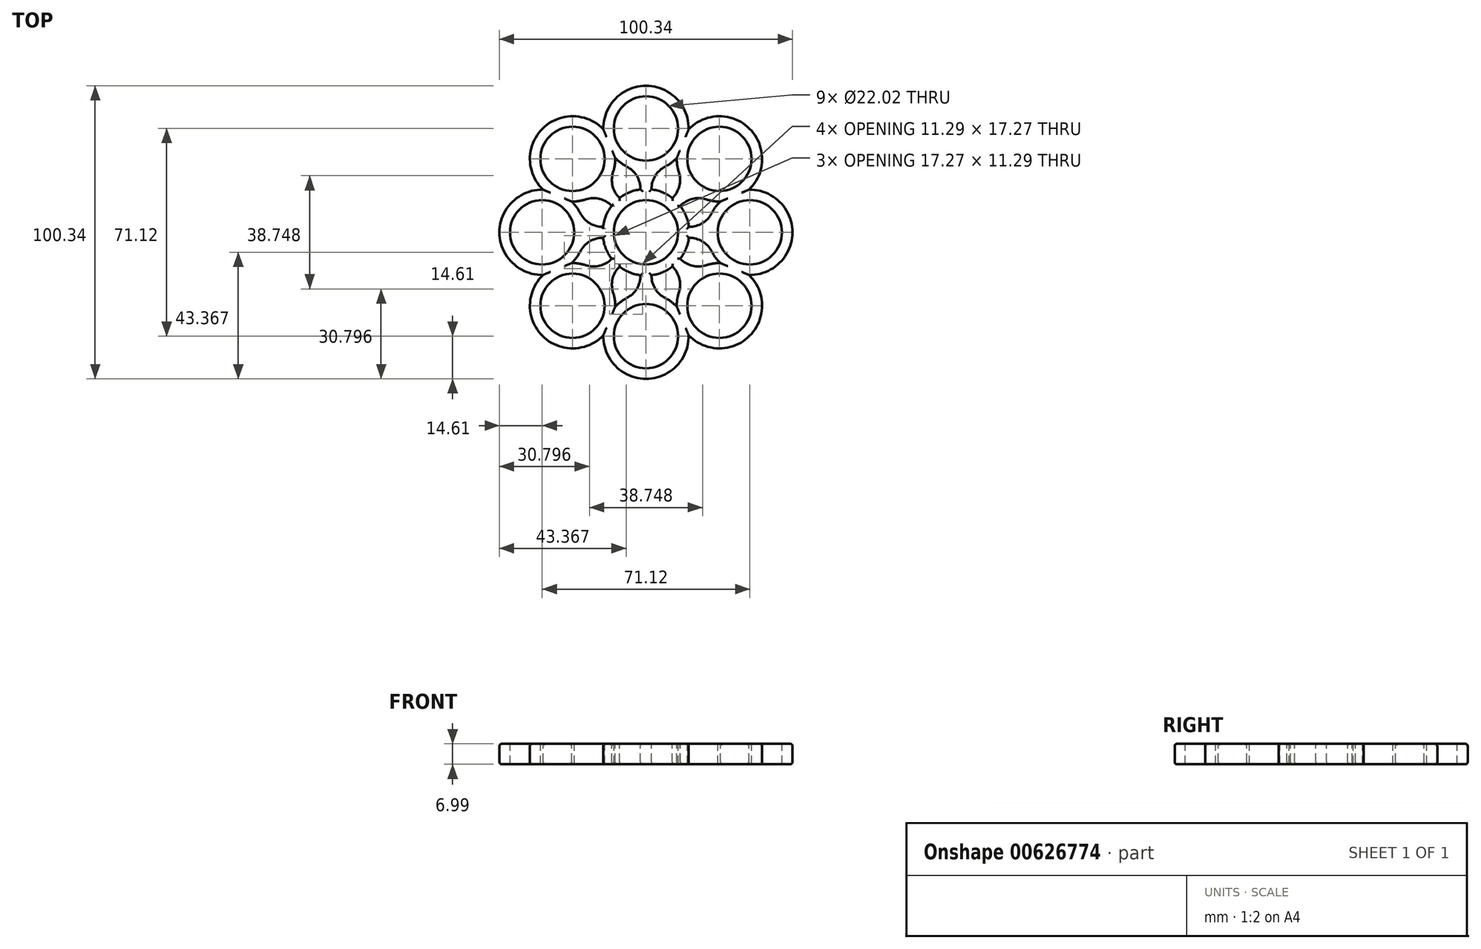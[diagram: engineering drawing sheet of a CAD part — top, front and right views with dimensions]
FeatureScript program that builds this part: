
annotation { "Feature Type Name" : "Feature", "Feature Type Description" : "" }
export const myFeature = defineFeature(function(context is Context, id is Id, definition is map)
    precondition{}
    {
        {
            var Q0;
            Q0=qCreatedBy(makeId("Top.planeOp"),FACE);
            var sketch = newSketch(context, id + "F0", { "sketchPlane" : qUnion([Q0])});
            skCircle(sketch, "E0", {"center": v(0, 0) * mm, "radius": 11.01 * mm});
            skLineSegment(sketch, "E1", {"start": v(0, 0) * mm, "end": v(0, -35.56) * mm});
            skLineSegment(sketch, "E2", {"start": v(0, 0) * mm, "end": v(0, 35.56) * mm});
            skLineSegment(sketch, "E3", {"start": v(0, 0) * mm, "end": v(25.14, 25.14) * mm});
            skLineSegment(sketch, "E4", {"start": v(0, 0) * mm, "end": v(-25.14, -25.14) * mm});
            skLineSegment(sketch, "E5", {"start": v(0, 0) * mm, "end": v(25.14, -25.14) * mm});
            skLineSegment(sketch, "E6", {"start": v(0, 0) * mm, "end": v(-25.14, 25.14) * mm});
            skLineSegment(sketch, "E7", {"start": v(0, 0) * mm, "end": v(35.56, 0) * mm});
            skLineSegment(sketch, "E8", {"start": v(0, 0) * mm, "end": v(-35.56, 0) * mm});
            skCircle(sketch, "E9", {"center": v(0, 35.56) * mm, "radius": 11.01 * mm});
            skCircle(sketch, "E10", {"center": v(25.14, 25.14) * mm, "radius": 11.01 * mm});
            skCircle(sketch, "E11", {"center": v(35.56, 0) * mm, "radius": 11.01 * mm});
            skCircle(sketch, "E12", {"center": v(25.14, -25.14) * mm, "radius": 11.01 * mm});
            skCircle(sketch, "E13", {"center": v(0, -35.56) * mm, "radius": 11.01 * mm});
            skCircle(sketch, "E14", {"center": v(-25.14, -25.14) * mm, "radius": 11.01 * mm});
            skCircle(sketch, "E15", {"center": v(-35.56, 0) * mm, "radius": 11.01 * mm});
            skCircle(sketch, "E16", {"center": v(-25.14, 25.14) * mm, "radius": 11.01 * mm});
            skCircle(sketch, "E17", {"center": v(0, 35.56) * mm, "radius": 14.6 * mm});
            skCircle(sketch, "E18", {"center": v(-25.14, 25.14) * mm, "radius": 14.6 * mm});
            skCircle(sketch, "E19", {"center": v(25.14, 25.14) * mm, "radius": 14.6 * mm});
            skCircle(sketch, "E20", {"center": v(35.56, 0) * mm, "radius": 14.6 * mm});
            skCircle(sketch, "E21", {"center": v(25.14, -25.14) * mm, "radius": 14.6 * mm});
            skCircle(sketch, "E22", {"center": v(0, -35.56) * mm, "radius": 14.6 * mm});
            skCircle(sketch, "E23", {"center": v(-35.56, 0) * mm, "radius": 14.6 * mm});
            skCircle(sketch, "E24", {"center": v(-25.14, -25.14) * mm, "radius": 14.6 * mm});
            skCircle(sketch, "E25", {"center": v(0, 0) * mm, "radius": 14.82 * mm});
            skArc(sketch, "E26", {"start": v(-11.74, 9.05) * mm, "mid": v(-15.85, 11.43) * mm, "end": v(-20.6, 11.26) * mm});
            skArc(sketch, "E27", {"start": v(-11.26, 20.6) * mm, "mid": v(-11.43, 15.85) * mm, "end": v(-9.05, 11.74) * mm});
            skArc(sketch, "E28.1.0", {"start": v(-22.53, 6.6) * mm, "mid": v(-19.3, 3.13) * mm, "end": v(-14.7, 1.9) * mm});
            skArc(sketch, "E28.1.1", {"start": v(-14.7, -1.9) * mm, "mid": v(-19.3, -3.13) * mm, "end": v(-22.53, -6.6) * mm});
            skArc(sketch, "E28.2.0", {"start": v(-20.6, -11.26) * mm, "mid": v(-15.85, -11.43) * mm, "end": v(-11.74, -9.05) * mm});
            skArc(sketch, "E28.2.1", {"start": v(-9.05, -11.74) * mm, "mid": v(-11.43, -15.85) * mm, "end": v(-11.26, -20.6) * mm});
            skArc(sketch, "E28.3.0", {"start": v(-6.6, -22.53) * mm, "mid": v(-3.13, -19.3) * mm, "end": v(-1.9, -14.7) * mm});
            skArc(sketch, "E28.3.1", {"start": v(1.9, -14.7) * mm, "mid": v(3.13, -19.3) * mm, "end": v(6.6, -22.53) * mm});
            skArc(sketch, "E28.4.0", {"start": v(11.26, -20.6) * mm, "mid": v(11.43, -15.85) * mm, "end": v(9.05, -11.74) * mm});
            skArc(sketch, "E28.4.1", {"start": v(11.74, -9.05) * mm, "mid": v(15.85, -11.43) * mm, "end": v(20.6, -11.26) * mm});
            skArc(sketch, "E28.5.0", {"start": v(22.53, -6.6) * mm, "mid": v(19.3, -3.13) * mm, "end": v(14.7, -1.9) * mm});
            skArc(sketch, "E28.5.1", {"start": v(14.7, 1.9) * mm, "mid": v(19.3, 3.13) * mm, "end": v(22.53, 6.6) * mm});
            skArc(sketch, "E28.6.0", {"start": v(20.6, 11.26) * mm, "mid": v(15.85, 11.43) * mm, "end": v(11.74, 9.05) * mm});
            skArc(sketch, "E28.6.1", {"start": v(9.05, 11.74) * mm, "mid": v(11.43, 15.85) * mm, "end": v(11.26, 20.6) * mm});
            skArc(sketch, "E28.7.0", {"start": v(6.6, 22.53) * mm, "mid": v(3.13, 19.3) * mm, "end": v(1.9, 14.7) * mm});
            skArc(sketch, "E28.7.1", {"start": v(-1.9, 14.7) * mm, "mid": v(-3.13, 19.3) * mm, "end": v(-6.6, 22.53) * mm});
            skSolve(sketch);
        }
        {
            var Q0;
            Q0 = qSketchRegion(id + "F0", true);
            var Q1;
            {var subQ1=sQuery(id+"F0.wireOp",EDGE,"E0");var subQ5=sQuery(id+"F0.wireOp",EDGE,"E2");var subQ6=makeQuery(id+"F0.imprint","INTERSECT",VERTEX,{"derivedFrom":[subQ1,subQ5]});Q1=makeQuery(id+"F0.imprint","IMPRINT",FACE,{"disambiguationData":[TD([[makeQuery(id+"F0.imprint","IMPRINT",EDGE,{"disambiguationData":[TD([[subQ6,-1.0]])],"derivedFrom":subQ1}),-1.0]])]});}
            var Q2;
            {var subQ2=sQuery(id+"F0.wireOp",EDGE,"E3");var subQ4=sQuery(id+"F0.wireOp",EDGE,"E0");var subQ5=makeQuery(id+"F0.imprint","INTERSECT",VERTEX,{"derivedFrom":[subQ4,subQ2]});Q2=makeQuery(id+"F0.imprint","IMPRINT",FACE,{"disambiguationData":[TD([[makeQuery(id+"F0.imprint","IMPRINT",EDGE,{"disambiguationData":[TD([[subQ5,-1.0]])],"derivedFrom":subQ4}),-1.0]])]});}
            var Q3;
            {var subQ5=sQuery(id+"F0.wireOp",EDGE,"E28.6.0");Q3=makeQuery(id+"F0.imprint","IMPRINT",FACE,{"disambiguationData":[TD([[makeQuery(id+"F0.imprint","IMPRINT",EDGE,{"derivedFrom":subQ5}),-1.0]])]});}
            var Q4;
            {var subQ5=sQuery(id+"F0.wireOp",EDGE,"E28.6.1");Q4=makeQuery(id+"F0.imprint","IMPRINT",FACE,{"disambiguationData":[TD([[makeQuery(id+"F0.imprint","IMPRINT",EDGE,{"derivedFrom":subQ5}),-1.0]])]});}
            var Q5;
            {var subQ5=sQuery(id+"F0.wireOp",EDGE,"E28.5.1");Q5=makeQuery(id+"F0.imprint","IMPRINT",FACE,{"disambiguationData":[TD([[makeQuery(id+"F0.imprint","IMPRINT",EDGE,{"derivedFrom":subQ5}),-1.0]])]});}
            var Q6;
            {var subQ5=sQuery(id+"F0.wireOp",EDGE,"E28.5.0");Q6=makeQuery(id+"F0.imprint","IMPRINT",FACE,{"disambiguationData":[TD([[makeQuery(id+"F0.imprint","IMPRINT",EDGE,{"derivedFrom":subQ5}),-1.0]])]});}
            var Q7;
            {var subQ1=sQuery(id+"F0.wireOp",EDGE,"E0");var subQ6=sQuery(id+"F0.wireOp",EDGE,"E7");var subQ7=makeQuery(id+"F0.imprint","INTERSECT",VERTEX,{"derivedFrom":[subQ1,subQ6]});Q7=makeQuery(id+"F0.imprint","IMPRINT",FACE,{"disambiguationData":[TD([[makeQuery(id+"F0.imprint","IMPRINT",EDGE,{"disambiguationData":[TD([[subQ7,1.0]])],"derivedFrom":subQ1}),-1.0]])]});}
            var Q8;
            {var subQ4=sQuery(id+"F0.wireOp",EDGE,"E0");var subQ6=sQuery(id+"F0.wireOp",EDGE,"E3");var subQ7=makeQuery(id+"F0.imprint","INTERSECT",VERTEX,{"derivedFrom":[subQ4,subQ6]});Q8=makeQuery(id+"F0.imprint","IMPRINT",FACE,{"disambiguationData":[TD([[makeQuery(id+"F0.imprint","IMPRINT",EDGE,{"disambiguationData":[TD([[subQ7,1.0]])],"derivedFrom":subQ4}),-1.0]])]});}
            var Q9;
            {var subQ5=sQuery(id+"F0.wireOp",EDGE,"E28.4.1");Q9=makeQuery(id+"F0.imprint","IMPRINT",FACE,{"disambiguationData":[TD([[makeQuery(id+"F0.imprint","IMPRINT",EDGE,{"derivedFrom":subQ5}),-1.0]])]});}
            var Q10;
            {var subQ5=sQuery(id+"F0.wireOp",EDGE,"E28.4.0");Q10=makeQuery(id+"F0.imprint","IMPRINT",FACE,{"disambiguationData":[TD([[makeQuery(id+"F0.imprint","IMPRINT",EDGE,{"derivedFrom":subQ5}),-1.0]])]});}
            var Q11;
            {var subQ5=sQuery(id+"F0.wireOp",EDGE,"E28.3.1");Q11=makeQuery(id+"F0.imprint","IMPRINT",FACE,{"disambiguationData":[TD([[makeQuery(id+"F0.imprint","IMPRINT",EDGE,{"derivedFrom":subQ5}),-1.0]])]});}
            var Q12;
            {var subQ5=sQuery(id+"F0.wireOp",EDGE,"E28.3.0");Q12=makeQuery(id+"F0.imprint","IMPRINT",FACE,{"disambiguationData":[TD([[makeQuery(id+"F0.imprint","IMPRINT",EDGE,{"derivedFrom":subQ5}),-1.0]])]});}
            var Q13;
            {var subQ5=sQuery(id+"F0.wireOp",EDGE,"E28.2.1");Q13=makeQuery(id+"F0.imprint","IMPRINT",FACE,{"disambiguationData":[TD([[makeQuery(id+"F0.imprint","IMPRINT",EDGE,{"derivedFrom":subQ5}),-1.0]])]});}
            var Q14;
            {var subQ5=sQuery(id+"F0.wireOp",EDGE,"E28.2.0");Q14=makeQuery(id+"F0.imprint","IMPRINT",FACE,{"disambiguationData":[TD([[makeQuery(id+"F0.imprint","IMPRINT",EDGE,{"derivedFrom":subQ5}),-1.0]])]});}
            var Q15;
            {var subQ5=sQuery(id+"F0.wireOp",EDGE,"E28.1.1");Q15=makeQuery(id+"F0.imprint","IMPRINT",FACE,{"disambiguationData":[TD([[makeQuery(id+"F0.imprint","IMPRINT",EDGE,{"derivedFrom":subQ5}),-1.0]])]});}
            var Q16;
            {var subQ5=sQuery(id+"F0.wireOp",EDGE,"E28.1.0");Q16=makeQuery(id+"F0.imprint","IMPRINT",FACE,{"disambiguationData":[TD([[makeQuery(id+"F0.imprint","IMPRINT",EDGE,{"derivedFrom":subQ5}),-1.0]])]});}
            var Q17;
            {var subQ5=sQuery(id+"F0.wireOp",EDGE,"E26");Q17=makeQuery(id+"F0.imprint","IMPRINT",FACE,{"disambiguationData":[TD([[makeQuery(id+"F0.imprint","IMPRINT",EDGE,{"derivedFrom":subQ5}),-1.0]])]});}
            var Q18;
            {var subQ5=sQuery(id+"F0.wireOp",EDGE,"E27");Q18=makeQuery(id+"F0.imprint","IMPRINT",FACE,{"disambiguationData":[TD([[makeQuery(id+"F0.imprint","IMPRINT",EDGE,{"derivedFrom":subQ5}),-1.0]])]});}
            var Q19;
            {var subQ5=sQuery(id+"F0.wireOp",EDGE,"E28.7.1");Q19=makeQuery(id+"F0.imprint","IMPRINT",FACE,{"disambiguationData":[TD([[makeQuery(id+"F0.imprint","IMPRINT",EDGE,{"derivedFrom":subQ5}),-1.0]])]});}
            var Q20;
            {var subQ2=sQuery(id+"F0.wireOp",EDGE,"E6");var subQ5=sQuery(id+"F0.wireOp",EDGE,"E0");var subQ9=makeQuery(id+"F0.imprint","INTERSECT",VERTEX,{"derivedFrom":[subQ5,subQ2]});Q20=makeQuery(id+"F0.imprint","IMPRINT",FACE,{"disambiguationData":[TD([[makeQuery(id+"F0.imprint","IMPRINT",EDGE,{"disambiguationData":[TD([[subQ9,-1.0]])],"derivedFrom":subQ5}),-1.0]])]});}
            var Q21;
            {var subQ0=sQuery(id+"F0.wireOp",EDGE,"E8");var subQ1=sQuery(id+"F0.wireOp",EDGE,"E0");var subQ2=makeQuery(id+"F0.imprint","INTERSECT",VERTEX,{"derivedFrom":[subQ1,subQ0]});Q21=makeQuery(id+"F0.imprint","IMPRINT",FACE,{"disambiguationData":[TD([[makeQuery(id+"F0.imprint","IMPRINT",EDGE,{"disambiguationData":[TD([[subQ2,-1.0]])],"derivedFrom":subQ1}),-1.0]])]});}
            var Q22;
            {var subQ2=sQuery(id+"F0.wireOp",EDGE,"E4");var subQ4=sQuery(id+"F0.wireOp",EDGE,"E0");var subQ5=makeQuery(id+"F0.imprint","INTERSECT",VERTEX,{"derivedFrom":[subQ4,subQ2]});Q22=makeQuery(id+"F0.imprint","IMPRINT",FACE,{"disambiguationData":[TD([[makeQuery(id+"F0.imprint","IMPRINT",EDGE,{"disambiguationData":[TD([[subQ5,-1.0]])],"derivedFrom":subQ4}),-1.0]])]});}
            var Q23;
            {var subQ2=sQuery(id+"F0.wireOp",EDGE,"E1");var subQ4=sQuery(id+"F0.wireOp",EDGE,"E0");var subQ5=makeQuery(id+"F0.imprint","INTERSECT",VERTEX,{"derivedFrom":[subQ4,subQ2]});Q23=makeQuery(id+"F0.imprint","IMPRINT",FACE,{"disambiguationData":[TD([[makeQuery(id+"F0.imprint","IMPRINT",EDGE,{"disambiguationData":[TD([[subQ5,-1.0]])],"derivedFrom":subQ4}),-1.0]])]});}
            var Q24;
            {var subQ5=sQuery(id+"F0.wireOp",EDGE,"E28.7.0");Q24=makeQuery(id+"F0.imprint","IMPRINT",FACE,{"disambiguationData":[TD([[makeQuery(id+"F0.imprint","IMPRINT",EDGE,{"derivedFrom":subQ5}),-1.0]])]});}
            extrude(context, id + "F1", {"entities" : qUnion([Q0, Q1, Q2, Q3, Q4, Q5, Q6, Q7, Q8, Q9, Q10, Q11, Q12, Q13, Q14, Q15, Q16, Q17, Q18, Q19, Q20, Q21, Q22, Q23, Q24]), "oppositeDirection" : true, "depth" : 7 * mm, "offsetDistance" : 25.4 * mm});
        }
        {
            var Q0;
            {var subQ0=sQuery(id+"F0.wireOp",EDGE,"E18");Q0=makeQuery(id+"F1.opExtrude","CAP_EDGE",EDGE,{"disambiguationData":[OSD([subQ0]),TDD([makeQuery(id+"F0.imprint","IMPRINT",EDGE,{"disambiguationData":[TD([[makeQuery(id+"F0.imprint","INTERSECT",VERTEX,{"disambiguationData":[OD(0.0)],"derivedFrom":[sQuery(id+"F0.wireOp",EDGE,"E17"),subQ0]}),-1.0]])],"derivedFrom":subQ0})])],"isStart":true});}
            var Q1;
            {var subQ0=sQuery(id+"F0.wireOp",EDGE,"E17");Q1=makeQuery(id+"F1.opExtrude","CAP_EDGE",EDGE,{"disambiguationData":[OSD([subQ0]),TDD([makeQuery(id+"F0.imprint","IMPRINT",EDGE,{"disambiguationData":[TD([[makeQuery(id+"F0.imprint","INTERSECT",VERTEX,{"disambiguationData":[OD(0.0)],"derivedFrom":[subQ0,sQuery(id+"F0.wireOp",EDGE,"E18")]}),1.0]])],"derivedFrom":subQ0})])],"isStart":true});}
            var Q2;
            {var subQ0=sQuery(id+"F0.wireOp",EDGE,"E19");Q2=makeQuery(id+"F1.opExtrude","CAP_EDGE",EDGE,{"disambiguationData":[OSD([subQ0]),TDD([makeQuery(id+"F0.imprint","IMPRINT",EDGE,{"disambiguationData":[TD([[makeQuery(id+"F0.imprint","INTERSECT",VERTEX,{"disambiguationData":[OD(0.0)],"derivedFrom":[sQuery(id+"F0.wireOp",EDGE,"E17"),subQ0]}),1.0]])],"derivedFrom":subQ0})])],"isStart":true});}
            var Q3;
            {var subQ0=sQuery(id+"F0.wireOp",EDGE,"E20");Q3=makeQuery(id+"F1.opExtrude","CAP_EDGE",EDGE,{"disambiguationData":[OSD([subQ0]),TDD([makeQuery(id+"F0.imprint","IMPRINT",EDGE,{"disambiguationData":[TD([[makeQuery(id+"F0.imprint","INTERSECT",VERTEX,{"disambiguationData":[OD(0.0)],"derivedFrom":[sQuery(id+"F0.wireOp",EDGE,"E19"),subQ0]}),1.0]])],"derivedFrom":subQ0})])],"isStart":true});}
            var Q4;
            {var subQ0=sQuery(id+"F0.wireOp",EDGE,"E21");Q4=makeQuery(id+"F1.opExtrude","CAP_EDGE",EDGE,{"disambiguationData":[OSD([subQ0]),TDD([makeQuery(id+"F0.imprint","IMPRINT",EDGE,{"disambiguationData":[TD([[makeQuery(id+"F0.imprint","INTERSECT",VERTEX,{"disambiguationData":[OD(0.0)],"derivedFrom":[sQuery(id+"F0.wireOp",EDGE,"E20"),subQ0]}),1.0]])],"derivedFrom":subQ0})])],"isStart":true});}
            var Q5;
            {var subQ0=sQuery(id+"F0.wireOp",EDGE,"E22");Q5=makeQuery(id+"F1.opExtrude","CAP_EDGE",EDGE,{"disambiguationData":[OSD([subQ0]),TDD([makeQuery(id+"F0.imprint","IMPRINT",EDGE,{"disambiguationData":[TD([[makeQuery(id+"F0.imprint","INTERSECT",VERTEX,{"disambiguationData":[OD(0.0)],"derivedFrom":[sQuery(id+"F0.wireOp",EDGE,"E21"),subQ0]}),1.0]])],"derivedFrom":subQ0})])],"isStart":true});}
            var Q6;
            {var subQ0=sQuery(id+"F0.wireOp",EDGE,"E24");Q6=makeQuery(id+"F1.opExtrude","CAP_EDGE",EDGE,{"disambiguationData":[OSD([subQ0]),TDD([makeQuery(id+"F0.imprint","IMPRINT",EDGE,{"disambiguationData":[TD([[makeQuery(id+"F0.imprint","INTERSECT",VERTEX,{"disambiguationData":[OD(0.0)],"derivedFrom":[sQuery(id+"F0.wireOp",EDGE,"E22"),subQ0]}),1.0]])],"derivedFrom":subQ0})])],"isStart":true});}
            var Q7;
            {var subQ0=sQuery(id+"F0.wireOp",EDGE,"E23");Q7=makeQuery(id+"F1.opExtrude","CAP_EDGE",EDGE,{"disambiguationData":[OSD([subQ0]),TDD([makeQuery(id+"F0.imprint","IMPRINT",EDGE,{"disambiguationData":[TD([[makeQuery(id+"F0.imprint","INTERSECT",VERTEX,{"disambiguationData":[OD(0.0)],"derivedFrom":[sQuery(id+"F0.wireOp",EDGE,"E18"),subQ0]}),-1.0]])],"derivedFrom":subQ0})])],"isStart":true});}
            fillet(context, id + "F2", {"entities" : qUnion([Q0, Q1, Q2, Q3, Q4, Q5, Q6, Q7]), "radius" : 0.76 * mm, "tangentPropagation" : true, "allowEdgeOverflow" : false});
        }
        {
            var Q0;
            {var subQ0=sQuery(id+"F0.wireOp",EDGE,"E21");Q0=makeQuery(id+"F1.opExtrude","CAP_EDGE",EDGE,{"disambiguationData":[OSD([subQ0]),TDD([makeQuery(id+"F0.imprint","IMPRINT",EDGE,{"disambiguationData":[TD([[makeQuery(id+"F0.imprint","INTERSECT",VERTEX,{"disambiguationData":[OD(0.0)],"derivedFrom":[sQuery(id+"F0.wireOp",EDGE,"E20"),subQ0]}),1.0]])],"derivedFrom":subQ0})])],"isStart":false});}
            var Q1;
            {var subQ0=sQuery(id+"F0.wireOp",EDGE,"E20");Q1=makeQuery(id+"F1.opExtrude","CAP_EDGE",EDGE,{"disambiguationData":[OSD([subQ0]),TDD([makeQuery(id+"F0.imprint","IMPRINT",EDGE,{"disambiguationData":[TD([[makeQuery(id+"F0.imprint","INTERSECT",VERTEX,{"disambiguationData":[OD(0.0)],"derivedFrom":[sQuery(id+"F0.wireOp",EDGE,"E19"),subQ0]}),1.0]])],"derivedFrom":subQ0})])],"isStart":false});}
            var Q2;
            {var subQ0=sQuery(id+"F0.wireOp",EDGE,"E19");Q2=makeQuery(id+"F1.opExtrude","CAP_EDGE",EDGE,{"disambiguationData":[OSD([subQ0]),TDD([makeQuery(id+"F0.imprint","IMPRINT",EDGE,{"disambiguationData":[TD([[makeQuery(id+"F0.imprint","INTERSECT",VERTEX,{"disambiguationData":[OD(0.0)],"derivedFrom":[sQuery(id+"F0.wireOp",EDGE,"E17"),subQ0]}),1.0]])],"derivedFrom":subQ0})])],"isStart":false});}
            var Q3;
            {var subQ0=sQuery(id+"F0.wireOp",EDGE,"E17");Q3=makeQuery(id+"F1.opExtrude","CAP_EDGE",EDGE,{"disambiguationData":[OSD([subQ0]),TDD([makeQuery(id+"F0.imprint","IMPRINT",EDGE,{"disambiguationData":[TD([[makeQuery(id+"F0.imprint","INTERSECT",VERTEX,{"disambiguationData":[OD(0.0)],"derivedFrom":[subQ0,sQuery(id+"F0.wireOp",EDGE,"E18")]}),1.0]])],"derivedFrom":subQ0})])],"isStart":false});}
            var Q4;
            {var subQ0=sQuery(id+"F0.wireOp",EDGE,"E18");Q4=makeQuery(id+"F1.opExtrude","CAP_EDGE",EDGE,{"disambiguationData":[OSD([subQ0]),TDD([makeQuery(id+"F0.imprint","IMPRINT",EDGE,{"disambiguationData":[TD([[makeQuery(id+"F0.imprint","INTERSECT",VERTEX,{"disambiguationData":[OD(0.0)],"derivedFrom":[sQuery(id+"F0.wireOp",EDGE,"E17"),subQ0]}),-1.0]])],"derivedFrom":subQ0})])],"isStart":false});}
            var Q5;
            {var subQ0=sQuery(id+"F0.wireOp",EDGE,"E23");Q5=makeQuery(id+"F1.opExtrude","CAP_EDGE",EDGE,{"disambiguationData":[OSD([subQ0]),TDD([makeQuery(id+"F0.imprint","IMPRINT",EDGE,{"disambiguationData":[TD([[makeQuery(id+"F0.imprint","INTERSECT",VERTEX,{"disambiguationData":[OD(0.0)],"derivedFrom":[sQuery(id+"F0.wireOp",EDGE,"E18"),subQ0]}),-1.0]])],"derivedFrom":subQ0})])],"isStart":false});}
            var Q6;
            {var subQ0=sQuery(id+"F0.wireOp",EDGE,"E24");Q6=makeQuery(id+"F1.opExtrude","CAP_EDGE",EDGE,{"disambiguationData":[OSD([subQ0]),TDD([makeQuery(id+"F0.imprint","IMPRINT",EDGE,{"disambiguationData":[TD([[makeQuery(id+"F0.imprint","INTERSECT",VERTEX,{"disambiguationData":[OD(0.0)],"derivedFrom":[sQuery(id+"F0.wireOp",EDGE,"E22"),subQ0]}),1.0]])],"derivedFrom":subQ0})])],"isStart":false});}
            var Q7;
            {var subQ0=sQuery(id+"F0.wireOp",EDGE,"E22");Q7=makeQuery(id+"F1.opExtrude","CAP_EDGE",EDGE,{"disambiguationData":[OSD([subQ0]),TDD([makeQuery(id+"F0.imprint","IMPRINT",EDGE,{"disambiguationData":[TD([[makeQuery(id+"F0.imprint","INTERSECT",VERTEX,{"disambiguationData":[OD(0.0)],"derivedFrom":[sQuery(id+"F0.wireOp",EDGE,"E21"),subQ0]}),1.0]])],"derivedFrom":subQ0})])],"isStart":false});}
            fillet(context, id + "F3", {"entities" : qUnion([Q0, Q1, Q2, Q3, Q4, Q5, Q6, Q7]), "radius" : 0.76 * mm, "tangentPropagation" : true, "allowEdgeOverflow" : false});
        }
        {
            var Q0;
            Q0=makeQuery(id+"F1.opExtrude","CAP_EDGE",EDGE,{"disambiguationData":[OSD([sQuery(id+"F0.wireOp",EDGE,"E28.7.1")])],"isStart":true});
            var Q1;
            {var subQ0=sQuery(id+"F0.wireOp",EDGE,"E17");Q1=makeQuery(id+"F1.opExtrude","CAP_EDGE",EDGE,{"disambiguationData":[OSD([subQ0]),TDD([makeQuery(id+"F0.imprint","IMPRINT",EDGE,{"disambiguationData":[TD([[makeQuery(id+"F0.imprint","INTERSECT",VERTEX,{"derivedFrom":[subQ0,sQuery(id+"F0.wireOp",EDGE,"E28.7.1")]}),1.0]])],"derivedFrom":subQ0})])],"isStart":true});}
            var Q2;
            {var subQ0=sQuery(id+"F0.wireOp",EDGE,"E18");Q2=makeQuery(id+"F1.opExtrude","CAP_EDGE",EDGE,{"disambiguationData":[OSD([subQ0]),TDD([makeQuery(id+"F0.imprint","IMPRINT",EDGE,{"disambiguationData":[TD([[makeQuery(id+"F0.imprint","INTERSECT",VERTEX,{"derivedFrom":[subQ0,sQuery(id+"F0.wireOp",EDGE,"E27")]}),-1.0]])],"derivedFrom":subQ0})])],"isStart":true});}
            var Q3;
            Q3=makeQuery(id+"F1.opExtrude","CAP_EDGE",EDGE,{"disambiguationData":[OSD([sQuery(id+"F0.wireOp",EDGE,"E27")])],"isStart":true});
            var Q4;
            {var subQ0=sQuery(id+"F0.wireOp",EDGE,"E25");Q4=makeQuery(id+"F1.opExtrude","CAP_EDGE",EDGE,{"disambiguationData":[OSD([subQ0]),TDD([makeQuery(id+"F0.imprint","IMPRINT",EDGE,{"disambiguationData":[TD([[makeQuery(id+"F0.imprint","INTERSECT",VERTEX,{"derivedFrom":[subQ0,sQuery(id+"F0.wireOp",EDGE,"E27")]}),1.0]])],"derivedFrom":subQ0})])],"isStart":true});}
            var Q5;
            Q5=makeQuery(id+"F1.opExtrude","CAP_EDGE",EDGE,{"disambiguationData":[OSD([sQuery(id+"F0.wireOp",EDGE,"E28.7.0")])],"isStart":false});
            var Q6;
            Q6=makeQuery(id+"F1.opExtrude","CAP_EDGE",EDGE,{"disambiguationData":[OSD([sQuery(id+"F0.wireOp",EDGE,"E28.7.0")])],"isStart":true});
            var Q7;
            {var subQ0=sQuery(id+"F0.wireOp",EDGE,"E17");Q7=makeQuery(id+"F1.opExtrude","CAP_EDGE",EDGE,{"disambiguationData":[OSD([subQ0]),TDD([makeQuery(id+"F0.imprint","IMPRINT",EDGE,{"disambiguationData":[TD([[makeQuery(id+"F0.imprint","INTERSECT",VERTEX,{"derivedFrom":[subQ0,sQuery(id+"F0.wireOp",EDGE,"E28.7.0")]}),-1.0]])],"derivedFrom":subQ0})])],"isStart":true});}
            var Q8;
            {var subQ0=sQuery(id+"F0.wireOp",EDGE,"E19");Q8=makeQuery(id+"F1.opExtrude","CAP_EDGE",EDGE,{"disambiguationData":[OSD([subQ0]),TDD([makeQuery(id+"F0.imprint","IMPRINT",EDGE,{"disambiguationData":[TD([[makeQuery(id+"F0.imprint","INTERSECT",VERTEX,{"derivedFrom":[subQ0,sQuery(id+"F0.wireOp",EDGE,"E28.6.1")]}),1.0]])],"derivedFrom":subQ0})])],"isStart":true});}
            var Q9;
            Q9=makeQuery(id+"F1.opExtrude","CAP_EDGE",EDGE,{"disambiguationData":[OSD([sQuery(id+"F0.wireOp",EDGE,"E28.6.1")])],"isStart":true});
            var Q10;
            {var subQ0=sQuery(id+"F0.wireOp",EDGE,"E25");Q10=makeQuery(id+"F1.opExtrude","CAP_EDGE",EDGE,{"disambiguationData":[OSD([subQ0]),TDD([makeQuery(id+"F0.imprint","IMPRINT",EDGE,{"disambiguationData":[TD([[makeQuery(id+"F0.imprint","INTERSECT",VERTEX,{"derivedFrom":[subQ0,sQuery(id+"F0.wireOp",EDGE,"E28.6.1")]}),-1.0]])],"derivedFrom":subQ0})])],"isStart":true});}
            var Q11;
            {var subQ0=sQuery(id+"F0.wireOp",EDGE,"E25");Q11=makeQuery(id+"F1.opExtrude","CAP_EDGE",EDGE,{"disambiguationData":[OSD([subQ0]),TDD([makeQuery(id+"F0.imprint","IMPRINT",EDGE,{"disambiguationData":[TD([[makeQuery(id+"F0.imprint","INTERSECT",VERTEX,{"derivedFrom":[subQ0,sQuery(id+"F0.wireOp",EDGE,"E28.5.1")]}),-1.0]])],"derivedFrom":subQ0})])],"isStart":true});}
            var Q12;
            {var subQ0=sQuery(id+"F0.wireOp",EDGE,"E25");Q12=makeQuery(id+"F1.opExtrude","CAP_EDGE",EDGE,{"disambiguationData":[OSD([subQ0]),TDD([makeQuery(id+"F0.imprint","IMPRINT",EDGE,{"disambiguationData":[TD([[makeQuery(id+"F0.imprint","INTERSECT",VERTEX,{"derivedFrom":[subQ0,sQuery(id+"F0.wireOp",EDGE,"E28.4.1")]}),-1.0]])],"derivedFrom":subQ0})])],"isStart":true});}
            var Q13;
            {var subQ0=sQuery(id+"F0.wireOp",EDGE,"E25");Q13=makeQuery(id+"F1.opExtrude","CAP_EDGE",EDGE,{"disambiguationData":[OSD([subQ0]),TDD([makeQuery(id+"F0.imprint","IMPRINT",EDGE,{"disambiguationData":[TD([[makeQuery(id+"F0.imprint","INTERSECT",VERTEX,{"derivedFrom":[subQ0,sQuery(id+"F0.wireOp",EDGE,"E28.3.1")]}),-1.0]])],"derivedFrom":subQ0})])],"isStart":true});}
            var Q14;
            {var subQ0=sQuery(id+"F0.wireOp",EDGE,"E25");Q14=makeQuery(id+"F1.opExtrude","CAP_EDGE",EDGE,{"disambiguationData":[OSD([subQ0]),TDD([makeQuery(id+"F0.imprint","IMPRINT",EDGE,{"disambiguationData":[TD([[makeQuery(id+"F0.imprint","INTERSECT",VERTEX,{"derivedFrom":[subQ0,sQuery(id+"F0.wireOp",EDGE,"E28.2.1")]}),-1.0]])],"derivedFrom":subQ0})])],"isStart":true});}
            var Q15;
            {var subQ0=sQuery(id+"F0.wireOp",EDGE,"E25");Q15=makeQuery(id+"F1.opExtrude","CAP_EDGE",EDGE,{"disambiguationData":[OSD([subQ0]),TDD([makeQuery(id+"F0.imprint","IMPRINT",EDGE,{"disambiguationData":[TD([[makeQuery(id+"F0.imprint","INTERSECT",VERTEX,{"derivedFrom":[subQ0,sQuery(id+"F0.wireOp",EDGE,"E28.1.1")]}),-1.0]])],"derivedFrom":subQ0})])],"isStart":true});}
            var Q16;
            {var subQ0=sQuery(id+"F0.wireOp",EDGE,"E25");Q16=makeQuery(id+"F1.opExtrude","CAP_EDGE",EDGE,{"disambiguationData":[OSD([subQ0]),TDD([makeQuery(id+"F0.imprint","IMPRINT",EDGE,{"disambiguationData":[TD([[makeQuery(id+"F0.imprint","INTERSECT",VERTEX,{"derivedFrom":[subQ0,sQuery(id+"F0.wireOp",EDGE,"E26")]}),-1.0]])],"derivedFrom":subQ0})])],"isStart":false});}
            var Q17;
            Q17=makeQuery(id+"F1.opExtrude","CAP_EDGE",EDGE,{"disambiguationData":[OSD([sQuery(id+"F0.wireOp",EDGE,"E26")])],"isStart":true});
            var Q18;
            {var subQ0=sQuery(id+"F0.wireOp",EDGE,"E18");Q18=makeQuery(id+"F1.opExtrude","CAP_EDGE",EDGE,{"disambiguationData":[OSD([subQ0]),TDD([makeQuery(id+"F0.imprint","IMPRINT",EDGE,{"disambiguationData":[TD([[makeQuery(id+"F0.imprint","INTERSECT",VERTEX,{"derivedFrom":[subQ0,sQuery(id+"F0.wireOp",EDGE,"E26")]}),1.0]])],"derivedFrom":subQ0})])],"isStart":true});}
            var Q19;
            {var subQ0=sQuery(id+"F0.wireOp",EDGE,"E23");Q19=makeQuery(id+"F1.opExtrude","CAP_EDGE",EDGE,{"disambiguationData":[OSD([subQ0]),TDD([makeQuery(id+"F0.imprint","IMPRINT",EDGE,{"disambiguationData":[TD([[makeQuery(id+"F0.imprint","INTERSECT",VERTEX,{"derivedFrom":[subQ0,sQuery(id+"F0.wireOp",EDGE,"E28.1.0")]}),-1.0]])],"derivedFrom":subQ0})])],"isStart":true});}
            var Q20;
            Q20=makeQuery(id+"F1.opExtrude","CAP_EDGE",EDGE,{"disambiguationData":[OSD([sQuery(id+"F0.wireOp",EDGE,"E28.1.0")])],"isStart":true});
            var Q21;
            Q21=makeQuery(id+"F1.opExtrude","CAP_EDGE",EDGE,{"disambiguationData":[OSD([sQuery(id+"F0.wireOp",EDGE,"E28.1.1")])],"isStart":true});
            var Q22;
            {var subQ0=sQuery(id+"F0.wireOp",EDGE,"E23");Q22=makeQuery(id+"F1.opExtrude","CAP_EDGE",EDGE,{"disambiguationData":[OSD([subQ0]),TDD([makeQuery(id+"F0.imprint","IMPRINT",EDGE,{"disambiguationData":[TD([[makeQuery(id+"F0.imprint","INTERSECT",VERTEX,{"derivedFrom":[subQ0,sQuery(id+"F0.wireOp",EDGE,"E28.1.1")]}),1.0]])],"derivedFrom":subQ0})])],"isStart":true});}
            var Q23;
            {var subQ0=sQuery(id+"F0.wireOp",EDGE,"E24");Q23=makeQuery(id+"F1.opExtrude","CAP_EDGE",EDGE,{"disambiguationData":[OSD([subQ0]),TDD([makeQuery(id+"F0.imprint","IMPRINT",EDGE,{"disambiguationData":[TD([[makeQuery(id+"F0.imprint","INTERSECT",VERTEX,{"derivedFrom":[subQ0,sQuery(id+"F0.wireOp",EDGE,"E28.2.0")]}),-1.0]])],"derivedFrom":subQ0})])],"isStart":true});}
            var Q24;
            Q24=makeQuery(id+"F1.opExtrude","CAP_EDGE",EDGE,{"disambiguationData":[OSD([sQuery(id+"F0.wireOp",EDGE,"E28.2.0")])],"isStart":true});
            var Q25;
            Q25=makeQuery(id+"F1.opExtrude","CAP_EDGE",EDGE,{"disambiguationData":[OSD([sQuery(id+"F0.wireOp",EDGE,"E28.2.1")])],"isStart":true});
            var Q26;
            {var subQ0=sQuery(id+"F0.wireOp",EDGE,"E24");Q26=makeQuery(id+"F1.opExtrude","CAP_EDGE",EDGE,{"disambiguationData":[OSD([subQ0]),TDD([makeQuery(id+"F0.imprint","IMPRINT",EDGE,{"disambiguationData":[TD([[makeQuery(id+"F0.imprint","INTERSECT",VERTEX,{"derivedFrom":[subQ0,sQuery(id+"F0.wireOp",EDGE,"E28.2.1")]}),1.0]])],"derivedFrom":subQ0})])],"isStart":true});}
            var Q27;
            {var subQ0=sQuery(id+"F0.wireOp",EDGE,"E22");Q27=makeQuery(id+"F1.opExtrude","CAP_EDGE",EDGE,{"disambiguationData":[OSD([subQ0]),TDD([makeQuery(id+"F0.imprint","IMPRINT",EDGE,{"disambiguationData":[TD([[makeQuery(id+"F0.imprint","INTERSECT",VERTEX,{"derivedFrom":[subQ0,sQuery(id+"F0.wireOp",EDGE,"E28.3.0")]}),-1.0]])],"derivedFrom":subQ0})])],"isStart":true});}
            var Q28;
            Q28=makeQuery(id+"F1.opExtrude","CAP_EDGE",EDGE,{"disambiguationData":[OSD([sQuery(id+"F0.wireOp",EDGE,"E28.3.0")])],"isStart":true});
            var Q29;
            Q29=makeQuery(id+"F1.opExtrude","CAP_EDGE",EDGE,{"disambiguationData":[OSD([sQuery(id+"F0.wireOp",EDGE,"E28.3.1")])],"isStart":true});
            var Q30;
            {var subQ0=sQuery(id+"F0.wireOp",EDGE,"E22");Q30=makeQuery(id+"F1.opExtrude","CAP_EDGE",EDGE,{"disambiguationData":[OSD([subQ0]),TDD([makeQuery(id+"F0.imprint","IMPRINT",EDGE,{"disambiguationData":[TD([[makeQuery(id+"F0.imprint","INTERSECT",VERTEX,{"derivedFrom":[subQ0,sQuery(id+"F0.wireOp",EDGE,"E28.3.1")]}),1.0]])],"derivedFrom":subQ0})])],"isStart":true});}
            var Q31;
            {var subQ0=sQuery(id+"F0.wireOp",EDGE,"E21");Q31=makeQuery(id+"F1.opExtrude","CAP_EDGE",EDGE,{"disambiguationData":[OSD([subQ0]),TDD([makeQuery(id+"F0.imprint","IMPRINT",EDGE,{"disambiguationData":[TD([[makeQuery(id+"F0.imprint","INTERSECT",VERTEX,{"derivedFrom":[subQ0,sQuery(id+"F0.wireOp",EDGE,"E28.4.0")]}),-1.0]])],"derivedFrom":subQ0})])],"isStart":true});}
            var Q32;
            Q32=makeQuery(id+"F1.opExtrude","CAP_EDGE",EDGE,{"disambiguationData":[OSD([sQuery(id+"F0.wireOp",EDGE,"E28.4.0")])],"isStart":true});
            var Q33;
            {var subQ0=sQuery(id+"F0.wireOp",EDGE,"E21");Q33=makeQuery(id+"F1.opExtrude","CAP_EDGE",EDGE,{"disambiguationData":[OSD([subQ0]),TDD([makeQuery(id+"F0.imprint","IMPRINT",EDGE,{"disambiguationData":[TD([[makeQuery(id+"F0.imprint","INTERSECT",VERTEX,{"derivedFrom":[subQ0,sQuery(id+"F0.wireOp",EDGE,"E28.4.1")]}),1.0]])],"derivedFrom":subQ0})])],"isStart":true});}
            var Q34;
            {var subQ0=sQuery(id+"F0.wireOp",EDGE,"E20");Q34=makeQuery(id+"F1.opExtrude","CAP_EDGE",EDGE,{"disambiguationData":[OSD([subQ0]),TDD([makeQuery(id+"F0.imprint","IMPRINT",EDGE,{"disambiguationData":[TD([[makeQuery(id+"F0.imprint","INTERSECT",VERTEX,{"derivedFrom":[subQ0,sQuery(id+"F0.wireOp",EDGE,"E28.5.0")]}),-1.0]])],"derivedFrom":subQ0})])],"isStart":true});}
            var Q35;
            Q35=makeQuery(id+"F1.opExtrude","CAP_EDGE",EDGE,{"disambiguationData":[OSD([sQuery(id+"F0.wireOp",EDGE,"E28.5.0")])],"isStart":true});
            var Q36;
            Q36=makeQuery(id+"F1.opExtrude","CAP_EDGE",EDGE,{"disambiguationData":[OSD([sQuery(id+"F0.wireOp",EDGE,"E28.4.1")])],"isStart":true});
            var Q37;
            {var subQ0=sQuery(id+"F0.wireOp",EDGE,"E20");Q37=makeQuery(id+"F1.opExtrude","CAP_EDGE",EDGE,{"disambiguationData":[OSD([subQ0]),TDD([makeQuery(id+"F0.imprint","IMPRINT",EDGE,{"disambiguationData":[TD([[makeQuery(id+"F0.imprint","INTERSECT",VERTEX,{"derivedFrom":[subQ0,sQuery(id+"F0.wireOp",EDGE,"E28.5.1")]}),1.0]])],"derivedFrom":subQ0})])],"isStart":true});}
            var Q38;
            {var subQ0=sQuery(id+"F0.wireOp",EDGE,"E19");Q38=makeQuery(id+"F1.opExtrude","CAP_EDGE",EDGE,{"disambiguationData":[OSD([subQ0]),TDD([makeQuery(id+"F0.imprint","IMPRINT",EDGE,{"disambiguationData":[TD([[makeQuery(id+"F0.imprint","INTERSECT",VERTEX,{"derivedFrom":[subQ0,sQuery(id+"F0.wireOp",EDGE,"E28.6.0")]}),-1.0]])],"derivedFrom":subQ0})])],"isStart":true});}
            var Q39;
            Q39=makeQuery(id+"F1.opExtrude","CAP_EDGE",EDGE,{"disambiguationData":[OSD([sQuery(id+"F0.wireOp",EDGE,"E28.6.0")])],"isStart":true});
            var Q40;
            Q40=makeQuery(id+"F1.opExtrude","CAP_EDGE",EDGE,{"disambiguationData":[OSD([sQuery(id+"F0.wireOp",EDGE,"E28.5.1")])],"isStart":true});
            fillet(context, id + "F4", {"entities" : qUnion([Q0, Q1, Q2, Q3, Q4, Q5, Q6, Q7, Q8, Q9, Q10, Q11, Q12, Q13, Q14, Q15, Q16, Q17, Q18, Q19, Q20, Q21, Q22, Q23, Q24, Q25, Q26, Q27, Q28, Q29, Q30, Q31, Q32, Q33, Q34, Q35, Q36, Q37, Q38, Q39, Q40]), "radius" : 0.76 * mm, "tangentPropagation" : true, "allowEdgeOverflow" : false});
        }
        {
            var Q0;
            {var subQ0=sQuery(id+"F0.wireOp",EDGE,"E25");var subQ1=makeQuery(id+"F0.imprint","IMPRINT",EDGE,{"disambiguationData":[TD([[makeQuery(id+"F0.imprint","INTERSECT",VERTEX,{"derivedFrom":[subQ0,sQuery(id+"F0.wireOp",EDGE,"E26")]}),-1.0]])],"derivedFrom":subQ0});Q0=makeQuery(id+"F4.opFillet","BLEND_EDGE",EDGE,{"blendedFrom":[makeQuery(id+"F1.opExtrude","CAP_EDGE",EDGE,{"disambiguationData":[OSD([subQ0]),TDD([subQ1])],"isStart":false}),makeQuery(id+"F1.opExtrude","SWEPT_FACE",FACE,{"disambiguationData":[OSD([subQ0]),TDD([subQ1])]})],"blendedInto":[makeQuery(id+"F1.opExtrude","SWEPT_FACE",FACE,{"disambiguationData":[OSD([subQ0]),TDD([subQ1])]})]});}
            var Q1;
            {var subQ0=sQuery(id+"F0.wireOp",EDGE,"E25");Q1=makeQuery(id+"F1.opExtrude","CAP_EDGE",EDGE,{"disambiguationData":[OSD([subQ0]),TDD([makeQuery(id+"F0.imprint","IMPRINT",EDGE,{"disambiguationData":[TD([[makeQuery(id+"F0.imprint","INTERSECT",VERTEX,{"derivedFrom":[subQ0,sQuery(id+"F0.wireOp",EDGE,"E27")]}),1.0]])],"derivedFrom":subQ0})])],"isStart":false});}
            var Q2;
            {var subQ0=sQuery(id+"F0.wireOp",EDGE,"E25");Q2=makeQuery(id+"F1.opExtrude","CAP_EDGE",EDGE,{"disambiguationData":[OSD([subQ0]),TDD([makeQuery(id+"F0.imprint","IMPRINT",EDGE,{"disambiguationData":[TD([[makeQuery(id+"F0.imprint","INTERSECT",VERTEX,{"derivedFrom":[subQ0,sQuery(id+"F0.wireOp",EDGE,"E28.6.1")]}),-1.0]])],"derivedFrom":subQ0})])],"isStart":false});}
            var Q3;
            {var subQ0=sQuery(id+"F0.wireOp",EDGE,"E25");Q3=makeQuery(id+"F1.opExtrude","CAP_EDGE",EDGE,{"disambiguationData":[OSD([subQ0]),TDD([makeQuery(id+"F0.imprint","IMPRINT",EDGE,{"disambiguationData":[TD([[makeQuery(id+"F0.imprint","INTERSECT",VERTEX,{"derivedFrom":[subQ0,sQuery(id+"F0.wireOp",EDGE,"E28.5.1")]}),-1.0]])],"derivedFrom":subQ0})])],"isStart":false});}
            var Q4;
            {var subQ0=sQuery(id+"F0.wireOp",EDGE,"E25");Q4=makeQuery(id+"F1.opExtrude","CAP_EDGE",EDGE,{"disambiguationData":[OSD([subQ0]),TDD([makeQuery(id+"F0.imprint","IMPRINT",EDGE,{"disambiguationData":[TD([[makeQuery(id+"F0.imprint","INTERSECT",VERTEX,{"derivedFrom":[subQ0,sQuery(id+"F0.wireOp",EDGE,"E28.4.1")]}),-1.0]])],"derivedFrom":subQ0})])],"isStart":false});}
            var Q5;
            {var subQ0=sQuery(id+"F0.wireOp",EDGE,"E25");Q5=makeQuery(id+"F1.opExtrude","CAP_EDGE",EDGE,{"disambiguationData":[OSD([subQ0]),TDD([makeQuery(id+"F0.imprint","IMPRINT",EDGE,{"disambiguationData":[TD([[makeQuery(id+"F0.imprint","INTERSECT",VERTEX,{"derivedFrom":[subQ0,sQuery(id+"F0.wireOp",EDGE,"E28.3.1")]}),-1.0]])],"derivedFrom":subQ0})])],"isStart":false});}
            var Q6;
            {var subQ0=sQuery(id+"F0.wireOp",EDGE,"E25");Q6=makeQuery(id+"F1.opExtrude","CAP_EDGE",EDGE,{"disambiguationData":[OSD([subQ0]),TDD([makeQuery(id+"F0.imprint","IMPRINT",EDGE,{"disambiguationData":[TD([[makeQuery(id+"F0.imprint","INTERSECT",VERTEX,{"derivedFrom":[subQ0,sQuery(id+"F0.wireOp",EDGE,"E28.2.1")]}),-1.0]])],"derivedFrom":subQ0})])],"isStart":false});}
            var Q7;
            {var subQ0=sQuery(id+"F0.wireOp",EDGE,"E25");Q7=makeQuery(id+"F1.opExtrude","CAP_EDGE",EDGE,{"disambiguationData":[OSD([subQ0]),TDD([makeQuery(id+"F0.imprint","IMPRINT",EDGE,{"disambiguationData":[TD([[makeQuery(id+"F0.imprint","INTERSECT",VERTEX,{"derivedFrom":[subQ0,sQuery(id+"F0.wireOp",EDGE,"E28.1.1")]}),-1.0]])],"derivedFrom":subQ0})])],"isStart":false});}
            var Q8;
            Q8=makeQuery(id+"F1.opExtrude","CAP_EDGE",EDGE,{"disambiguationData":[OSD([sQuery(id+"F0.wireOp",EDGE,"E28.1.0")])],"isStart":false});
            var Q9;
            {var subQ0=sQuery(id+"F0.wireOp",EDGE,"E23");Q9=makeQuery(id+"F1.opExtrude","CAP_EDGE",EDGE,{"disambiguationData":[OSD([subQ0]),TDD([makeQuery(id+"F0.imprint","IMPRINT",EDGE,{"disambiguationData":[TD([[makeQuery(id+"F0.imprint","INTERSECT",VERTEX,{"derivedFrom":[subQ0,sQuery(id+"F0.wireOp",EDGE,"E28.1.0")]}),-1.0]])],"derivedFrom":subQ0})])],"isStart":false});}
            var Q10;
            {var subQ0=sQuery(id+"F0.wireOp",EDGE,"E18");Q10=makeQuery(id+"F1.opExtrude","CAP_EDGE",EDGE,{"disambiguationData":[OSD([subQ0]),TDD([makeQuery(id+"F0.imprint","IMPRINT",EDGE,{"disambiguationData":[TD([[makeQuery(id+"F0.imprint","INTERSECT",VERTEX,{"derivedFrom":[subQ0,sQuery(id+"F0.wireOp",EDGE,"E26")]}),1.0]])],"derivedFrom":subQ0})])],"isStart":false});}
            var Q11;
            Q11=makeQuery(id+"F1.opExtrude","CAP_EDGE",EDGE,{"disambiguationData":[OSD([sQuery(id+"F0.wireOp",EDGE,"E26")])],"isStart":false});
            var Q12;
            Q12=makeQuery(id+"F1.opExtrude","CAP_EDGE",EDGE,{"disambiguationData":[OSD([sQuery(id+"F0.wireOp",EDGE,"E28.1.1")])],"isStart":false});
            var Q13;
            {var subQ0=sQuery(id+"F0.wireOp",EDGE,"E23");Q13=makeQuery(id+"F1.opExtrude","CAP_EDGE",EDGE,{"disambiguationData":[OSD([subQ0]),TDD([makeQuery(id+"F0.imprint","IMPRINT",EDGE,{"disambiguationData":[TD([[makeQuery(id+"F0.imprint","INTERSECT",VERTEX,{"derivedFrom":[subQ0,sQuery(id+"F0.wireOp",EDGE,"E28.1.1")]}),1.0]])],"derivedFrom":subQ0})])],"isStart":false});}
            var Q14;
            {var subQ0=sQuery(id+"F0.wireOp",EDGE,"E24");Q14=makeQuery(id+"F1.opExtrude","CAP_EDGE",EDGE,{"disambiguationData":[OSD([subQ0]),TDD([makeQuery(id+"F0.imprint","IMPRINT",EDGE,{"disambiguationData":[TD([[makeQuery(id+"F0.imprint","INTERSECT",VERTEX,{"derivedFrom":[subQ0,sQuery(id+"F0.wireOp",EDGE,"E28.2.0")]}),-1.0]])],"derivedFrom":subQ0})])],"isStart":false});}
            var Q15;
            Q15=makeQuery(id+"F1.opExtrude","CAP_EDGE",EDGE,{"disambiguationData":[OSD([sQuery(id+"F0.wireOp",EDGE,"E28.2.0")])],"isStart":false});
            var Q16;
            Q16=makeQuery(id+"F1.opExtrude","CAP_EDGE",EDGE,{"disambiguationData":[OSD([sQuery(id+"F0.wireOp",EDGE,"E28.2.1")])],"isStart":false});
            var Q17;
            {var subQ0=sQuery(id+"F0.wireOp",EDGE,"E24");Q17=makeQuery(id+"F1.opExtrude","CAP_EDGE",EDGE,{"disambiguationData":[OSD([subQ0]),TDD([makeQuery(id+"F0.imprint","IMPRINT",EDGE,{"disambiguationData":[TD([[makeQuery(id+"F0.imprint","INTERSECT",VERTEX,{"derivedFrom":[subQ0,sQuery(id+"F0.wireOp",EDGE,"E28.2.1")]}),1.0]])],"derivedFrom":subQ0})])],"isStart":false});}
            var Q18;
            Q18=makeQuery(id+"F1.opExtrude","CAP_EDGE",EDGE,{"disambiguationData":[OSD([sQuery(id+"F0.wireOp",EDGE,"E28.3.0")])],"isStart":false});
            var Q19;
            Q19=makeQuery(id+"F1.opExtrude","CAP_EDGE",EDGE,{"disambiguationData":[OSD([sQuery(id+"F0.wireOp",EDGE,"E28.3.1")])],"isStart":false});
            var Q20;
            {var subQ0=sQuery(id+"F0.wireOp",EDGE,"E22");Q20=makeQuery(id+"F1.opExtrude","CAP_EDGE",EDGE,{"disambiguationData":[OSD([subQ0]),TDD([makeQuery(id+"F0.imprint","IMPRINT",EDGE,{"disambiguationData":[TD([[makeQuery(id+"F0.imprint","INTERSECT",VERTEX,{"derivedFrom":[subQ0,sQuery(id+"F0.wireOp",EDGE,"E28.3.1")]}),1.0]])],"derivedFrom":subQ0})])],"isStart":false});}
            var Q21;
            {var subQ0=sQuery(id+"F0.wireOp",EDGE,"E21");Q21=makeQuery(id+"F1.opExtrude","CAP_EDGE",EDGE,{"disambiguationData":[OSD([subQ0]),TDD([makeQuery(id+"F0.imprint","IMPRINT",EDGE,{"disambiguationData":[TD([[makeQuery(id+"F0.imprint","INTERSECT",VERTEX,{"derivedFrom":[subQ0,sQuery(id+"F0.wireOp",EDGE,"E28.4.0")]}),-1.0]])],"derivedFrom":subQ0})])],"isStart":false});}
            var Q22;
            Q22=makeQuery(id+"F1.opExtrude","CAP_EDGE",EDGE,{"disambiguationData":[OSD([sQuery(id+"F0.wireOp",EDGE,"E28.4.0")])],"isStart":false});
            var Q23;
            Q23=makeQuery(id+"F1.opExtrude","CAP_EDGE",EDGE,{"disambiguationData":[OSD([sQuery(id+"F0.wireOp",EDGE,"E28.4.1")])],"isStart":false});
            var Q24;
            Q24=makeQuery(id+"F1.opExtrude","CAP_EDGE",EDGE,{"disambiguationData":[OSD([sQuery(id+"F0.wireOp",EDGE,"E28.5.0")])],"isStart":false});
            var Q25;
            {var subQ0=sQuery(id+"F0.wireOp",EDGE,"E20");Q25=makeQuery(id+"F1.opExtrude","CAP_EDGE",EDGE,{"disambiguationData":[OSD([subQ0]),TDD([makeQuery(id+"F0.imprint","IMPRINT",EDGE,{"disambiguationData":[TD([[makeQuery(id+"F0.imprint","INTERSECT",VERTEX,{"derivedFrom":[subQ0,sQuery(id+"F0.wireOp",EDGE,"E28.5.0")]}),-1.0]])],"derivedFrom":subQ0})])],"isStart":false});}
            var Q26;
            {var subQ0=sQuery(id+"F0.wireOp",EDGE,"E22");Q26=makeQuery(id+"F1.opExtrude","CAP_EDGE",EDGE,{"disambiguationData":[OSD([subQ0]),TDD([makeQuery(id+"F0.imprint","IMPRINT",EDGE,{"disambiguationData":[TD([[makeQuery(id+"F0.imprint","INTERSECT",VERTEX,{"derivedFrom":[subQ0,sQuery(id+"F0.wireOp",EDGE,"E28.3.0")]}),-1.0]])],"derivedFrom":subQ0})])],"isStart":false});}
            var Q27;
            {var subQ0=sQuery(id+"F0.wireOp",EDGE,"E21");Q27=makeQuery(id+"F1.opExtrude","CAP_EDGE",EDGE,{"disambiguationData":[OSD([subQ0]),TDD([makeQuery(id+"F0.imprint","IMPRINT",EDGE,{"disambiguationData":[TD([[makeQuery(id+"F0.imprint","INTERSECT",VERTEX,{"derivedFrom":[subQ0,sQuery(id+"F0.wireOp",EDGE,"E28.4.1")]}),1.0]])],"derivedFrom":subQ0})])],"isStart":false});}
            var Q28;
            Q28=makeQuery(id+"F1.opExtrude","CAP_EDGE",EDGE,{"disambiguationData":[OSD([sQuery(id+"F0.wireOp",EDGE,"E28.5.1")])],"isStart":false});
            var Q29;
            {var subQ0=sQuery(id+"F0.wireOp",EDGE,"E20");Q29=makeQuery(id+"F1.opExtrude","CAP_EDGE",EDGE,{"disambiguationData":[OSD([subQ0]),TDD([makeQuery(id+"F0.imprint","IMPRINT",EDGE,{"disambiguationData":[TD([[makeQuery(id+"F0.imprint","INTERSECT",VERTEX,{"derivedFrom":[subQ0,sQuery(id+"F0.wireOp",EDGE,"E28.5.1")]}),1.0]])],"derivedFrom":subQ0})])],"isStart":false});}
            var Q30;
            {var subQ0=sQuery(id+"F0.wireOp",EDGE,"E19");var subQ1=makeQuery(id+"F0.imprint","IMPRINT",EDGE,{"disambiguationData":[TD([[makeQuery(id+"F0.imprint","INTERSECT",VERTEX,{"derivedFrom":[subQ0,sQuery(id+"F0.wireOp",EDGE,"E28.6.0")]}),-1.0]])],"derivedFrom":subQ0});Q30=makeQuery(id+"F4.opFillet","BLEND_EDGE",EDGE,{"blendedFrom":[makeQuery(id+"F1.opExtrude","CAP_EDGE",EDGE,{"disambiguationData":[OSD([subQ0]),TDD([subQ1])],"isStart":true}),makeQuery(id+"F1.opExtrude","SWEPT_FACE",FACE,{"disambiguationData":[OSD([subQ0]),TDD([subQ1])]})],"blendedInto":[makeQuery(id+"F1.opExtrude","SWEPT_FACE",FACE,{"disambiguationData":[OSD([subQ0]),TDD([subQ1])]})]});}
            var Q31;
            Q31=makeQuery(id+"F1.opExtrude","CAP_EDGE",EDGE,{"disambiguationData":[OSD([sQuery(id+"F0.wireOp",EDGE,"E28.6.0")])],"isStart":false});
            var Q32;
            Q32=makeQuery(id+"F1.opExtrude","CAP_EDGE",EDGE,{"disambiguationData":[OSD([sQuery(id+"F0.wireOp",EDGE,"E28.6.1")])],"isStart":false});
            var Q33;
            {var subQ0=sQuery(id+"F0.wireOp",EDGE,"E28.7.0");Q33=makeQuery(id+"F4.opFillet","BLEND_EDGE",EDGE,{"blendedFrom":[makeQuery(id+"F1.opExtrude","CAP_EDGE",EDGE,{"disambiguationData":[OSD([subQ0])],"isStart":false}),makeQuery(id+"F1.opExtrude","CAP_FACE",FACE,{"disambiguationData":[OSD([sQuery(id+"F0.wireOp",EDGE,"E0"),sQuery(id+"F0.wireOp",EDGE,"E9"),sQuery(id+"F0.wireOp",EDGE,"E10"),sQuery(id+"F0.wireOp",EDGE,"E11"),sQuery(id+"F0.wireOp",EDGE,"E12"),sQuery(id+"F0.wireOp",EDGE,"E13"),sQuery(id+"F0.wireOp",EDGE,"E14"),sQuery(id+"F0.wireOp",EDGE,"E15"),sQuery(id+"F0.wireOp",EDGE,"E16"),sQuery(id+"F0.wireOp",EDGE,"E17"),sQuery(id+"F0.wireOp",EDGE,"E18"),sQuery(id+"F0.wireOp",EDGE,"E19"),sQuery(id+"F0.wireOp",EDGE,"E20"),sQuery(id+"F0.wireOp",EDGE,"E21"),sQuery(id+"F0.wireOp",EDGE,"E22"),sQuery(id+"F0.wireOp",EDGE,"E23"),sQuery(id+"F0.wireOp",EDGE,"E24"),sQuery(id+"F0.wireOp",EDGE,"E25"),sQuery(id+"F0.wireOp",EDGE,"E26"),sQuery(id+"F0.wireOp",EDGE,"E27"),sQuery(id+"F0.wireOp",EDGE,"E28.1.0"),sQuery(id+"F0.wireOp",EDGE,"E28.1.1"),sQuery(id+"F0.wireOp",EDGE,"E28.2.0"),sQuery(id+"F0.wireOp",EDGE,"E28.2.1"),sQuery(id+"F0.wireOp",EDGE,"E28.3.0"),sQuery(id+"F0.wireOp",EDGE,"E28.3.1"),sQuery(id+"F0.wireOp",EDGE,"E28.4.0"),sQuery(id+"F0.wireOp",EDGE,"E28.4.1"),sQuery(id+"F0.wireOp",EDGE,"E28.5.0"),sQuery(id+"F0.wireOp",EDGE,"E28.5.1"),sQuery(id+"F0.wireOp",EDGE,"E28.6.0"),sQuery(id+"F0.wireOp",EDGE,"E28.6.1"),subQ0,sQuery(id+"F0.wireOp",EDGE,"E28.7.1")])],"isStart":false})],"blendedInto":[makeQuery(id+"F1.opExtrude","CAP_FACE",FACE,{"disambiguationData":[OSD([sQuery(id+"F0.wireOp",EDGE,"E0"),sQuery(id+"F0.wireOp",EDGE,"E9"),sQuery(id+"F0.wireOp",EDGE,"E10"),sQuery(id+"F0.wireOp",EDGE,"E11"),sQuery(id+"F0.wireOp",EDGE,"E12"),sQuery(id+"F0.wireOp",EDGE,"E13"),sQuery(id+"F0.wireOp",EDGE,"E14"),sQuery(id+"F0.wireOp",EDGE,"E15"),sQuery(id+"F0.wireOp",EDGE,"E16"),sQuery(id+"F0.wireOp",EDGE,"E17"),sQuery(id+"F0.wireOp",EDGE,"E18"),sQuery(id+"F0.wireOp",EDGE,"E19"),sQuery(id+"F0.wireOp",EDGE,"E20"),sQuery(id+"F0.wireOp",EDGE,"E21"),sQuery(id+"F0.wireOp",EDGE,"E22"),sQuery(id+"F0.wireOp",EDGE,"E23"),sQuery(id+"F0.wireOp",EDGE,"E24"),sQuery(id+"F0.wireOp",EDGE,"E25"),sQuery(id+"F0.wireOp",EDGE,"E26"),sQuery(id+"F0.wireOp",EDGE,"E27"),sQuery(id+"F0.wireOp",EDGE,"E28.1.0"),sQuery(id+"F0.wireOp",EDGE,"E28.1.1"),sQuery(id+"F0.wireOp",EDGE,"E28.2.0"),sQuery(id+"F0.wireOp",EDGE,"E28.2.1"),sQuery(id+"F0.wireOp",EDGE,"E28.3.0"),sQuery(id+"F0.wireOp",EDGE,"E28.3.1"),sQuery(id+"F0.wireOp",EDGE,"E28.4.0"),sQuery(id+"F0.wireOp",EDGE,"E28.4.1"),sQuery(id+"F0.wireOp",EDGE,"E28.5.0"),sQuery(id+"F0.wireOp",EDGE,"E28.5.1"),sQuery(id+"F0.wireOp",EDGE,"E28.6.0"),sQuery(id+"F0.wireOp",EDGE,"E28.6.1"),subQ0,sQuery(id+"F0.wireOp",EDGE,"E28.7.1")])],"isStart":false})]});}
            var Q34;
            {var subQ0=sQuery(id+"F0.wireOp",EDGE,"E28.7.0");var subQ1=sQuery(id+"F0.wireOp",EDGE,"E19");var subQ2=sQuery(id+"F0.wireOp",EDGE,"E17");Q34=makeQuery(id+"F4.opFillet","BLEND_EDGE",EDGE,{"blendedFrom":[makeQuery(id+"F1.opExtrude","CAP_EDGE",EDGE,{"disambiguationData":[OSD([subQ2]),TDD([makeQuery(id+"F0.imprint","IMPRINT",EDGE,{"disambiguationData":[TD([[makeQuery(id+"F0.imprint","INTERSECT",VERTEX,{"derivedFrom":[subQ2,subQ0]}),-1.0]])],"derivedFrom":subQ2})])],"isStart":false}),makeQuery(id+"F1.opExtrude","CAP_FACE",FACE,{"disambiguationData":[OSD([sQuery(id+"F0.wireOp",EDGE,"E0"),sQuery(id+"F0.wireOp",EDGE,"E9"),sQuery(id+"F0.wireOp",EDGE,"E10"),sQuery(id+"F0.wireOp",EDGE,"E11"),sQuery(id+"F0.wireOp",EDGE,"E12"),sQuery(id+"F0.wireOp",EDGE,"E13"),sQuery(id+"F0.wireOp",EDGE,"E14"),sQuery(id+"F0.wireOp",EDGE,"E15"),sQuery(id+"F0.wireOp",EDGE,"E16"),subQ2,sQuery(id+"F0.wireOp",EDGE,"E18"),subQ1,sQuery(id+"F0.wireOp",EDGE,"E20"),sQuery(id+"F0.wireOp",EDGE,"E21"),sQuery(id+"F0.wireOp",EDGE,"E22"),sQuery(id+"F0.wireOp",EDGE,"E23"),sQuery(id+"F0.wireOp",EDGE,"E24"),sQuery(id+"F0.wireOp",EDGE,"E25"),sQuery(id+"F0.wireOp",EDGE,"E26"),sQuery(id+"F0.wireOp",EDGE,"E27"),sQuery(id+"F0.wireOp",EDGE,"E28.1.0"),sQuery(id+"F0.wireOp",EDGE,"E28.1.1"),sQuery(id+"F0.wireOp",EDGE,"E28.2.0"),sQuery(id+"F0.wireOp",EDGE,"E28.2.1"),sQuery(id+"F0.wireOp",EDGE,"E28.3.0"),sQuery(id+"F0.wireOp",EDGE,"E28.3.1"),sQuery(id+"F0.wireOp",EDGE,"E28.4.0"),sQuery(id+"F0.wireOp",EDGE,"E28.4.1"),sQuery(id+"F0.wireOp",EDGE,"E28.5.0"),sQuery(id+"F0.wireOp",EDGE,"E28.5.1"),sQuery(id+"F0.wireOp",EDGE,"E28.6.0"),sQuery(id+"F0.wireOp",EDGE,"E28.6.1"),subQ0,sQuery(id+"F0.wireOp",EDGE,"E28.7.1")])],"isStart":false})],"blendedInto":[makeQuery(id+"F1.opExtrude","CAP_FACE",FACE,{"disambiguationData":[OSD([sQuery(id+"F0.wireOp",EDGE,"E0"),sQuery(id+"F0.wireOp",EDGE,"E9"),sQuery(id+"F0.wireOp",EDGE,"E10"),sQuery(id+"F0.wireOp",EDGE,"E11"),sQuery(id+"F0.wireOp",EDGE,"E12"),sQuery(id+"F0.wireOp",EDGE,"E13"),sQuery(id+"F0.wireOp",EDGE,"E14"),sQuery(id+"F0.wireOp",EDGE,"E15"),sQuery(id+"F0.wireOp",EDGE,"E16"),subQ2,sQuery(id+"F0.wireOp",EDGE,"E18"),subQ1,sQuery(id+"F0.wireOp",EDGE,"E20"),sQuery(id+"F0.wireOp",EDGE,"E21"),sQuery(id+"F0.wireOp",EDGE,"E22"),sQuery(id+"F0.wireOp",EDGE,"E23"),sQuery(id+"F0.wireOp",EDGE,"E24"),sQuery(id+"F0.wireOp",EDGE,"E25"),sQuery(id+"F0.wireOp",EDGE,"E26"),sQuery(id+"F0.wireOp",EDGE,"E27"),sQuery(id+"F0.wireOp",EDGE,"E28.1.0"),sQuery(id+"F0.wireOp",EDGE,"E28.1.1"),sQuery(id+"F0.wireOp",EDGE,"E28.2.0"),sQuery(id+"F0.wireOp",EDGE,"E28.2.1"),sQuery(id+"F0.wireOp",EDGE,"E28.3.0"),sQuery(id+"F0.wireOp",EDGE,"E28.3.1"),sQuery(id+"F0.wireOp",EDGE,"E28.4.0"),sQuery(id+"F0.wireOp",EDGE,"E28.4.1"),sQuery(id+"F0.wireOp",EDGE,"E28.5.0"),sQuery(id+"F0.wireOp",EDGE,"E28.5.1"),sQuery(id+"F0.wireOp",EDGE,"E28.6.0"),sQuery(id+"F0.wireOp",EDGE,"E28.6.1"),subQ0,sQuery(id+"F0.wireOp",EDGE,"E28.7.1")])],"isStart":false})]});}
            var Q35;
            {var subQ0=sQuery(id+"F0.wireOp",EDGE,"E19");Q35=makeQuery(id+"F1.opExtrude","CAP_EDGE",EDGE,{"disambiguationData":[OSD([subQ0]),TDD([makeQuery(id+"F0.imprint","IMPRINT",EDGE,{"disambiguationData":[TD([[makeQuery(id+"F0.imprint","INTERSECT",VERTEX,{"derivedFrom":[subQ0,sQuery(id+"F0.wireOp",EDGE,"E28.6.1")]}),1.0]])],"derivedFrom":subQ0})])],"isStart":false});}
            var Q36;
            Q36=makeQuery(id+"F1.opExtrude","CAP_EDGE",EDGE,{"disambiguationData":[OSD([sQuery(id+"F0.wireOp",EDGE,"E28.7.1")])],"isStart":false});
            var Q37;
            Q37=makeQuery(id+"F1.opExtrude","CAP_EDGE",EDGE,{"disambiguationData":[OSD([sQuery(id+"F0.wireOp",EDGE,"E27")])],"isStart":false});
            var Q38;
            {var subQ0=sQuery(id+"F0.wireOp",EDGE,"E18");Q38=makeQuery(id+"F1.opExtrude","CAP_EDGE",EDGE,{"disambiguationData":[OSD([subQ0]),TDD([makeQuery(id+"F0.imprint","IMPRINT",EDGE,{"disambiguationData":[TD([[makeQuery(id+"F0.imprint","INTERSECT",VERTEX,{"derivedFrom":[subQ0,sQuery(id+"F0.wireOp",EDGE,"E27")]}),-1.0]])],"derivedFrom":subQ0})])],"isStart":false});}
            var Q39;
            {var subQ0=sQuery(id+"F0.wireOp",EDGE,"E17");Q39=makeQuery(id+"F1.opExtrude","CAP_EDGE",EDGE,{"disambiguationData":[OSD([subQ0]),TDD([makeQuery(id+"F0.imprint","IMPRINT",EDGE,{"disambiguationData":[TD([[makeQuery(id+"F0.imprint","INTERSECT",VERTEX,{"derivedFrom":[subQ0,sQuery(id+"F0.wireOp",EDGE,"E28.7.1")]}),1.0]])],"derivedFrom":subQ0})])],"isStart":false});}
            fillet(context, id + "F5", {"entities" : qUnion([Q0, Q1, Q2, Q3, Q4, Q5, Q6, Q7, Q8, Q9, Q10, Q11, Q12, Q13, Q14, Q15, Q16, Q17, Q18, Q19, Q20, Q21, Q22, Q23, Q24, Q25, Q26, Q27, Q28, Q29, Q30, Q31, Q32, Q33, Q34, Q35, Q36, Q37, Q38, Q39]), "radius" : 0.76 * mm, "tangentPropagation" : true, "allowEdgeOverflow" : false});
        }
    });
